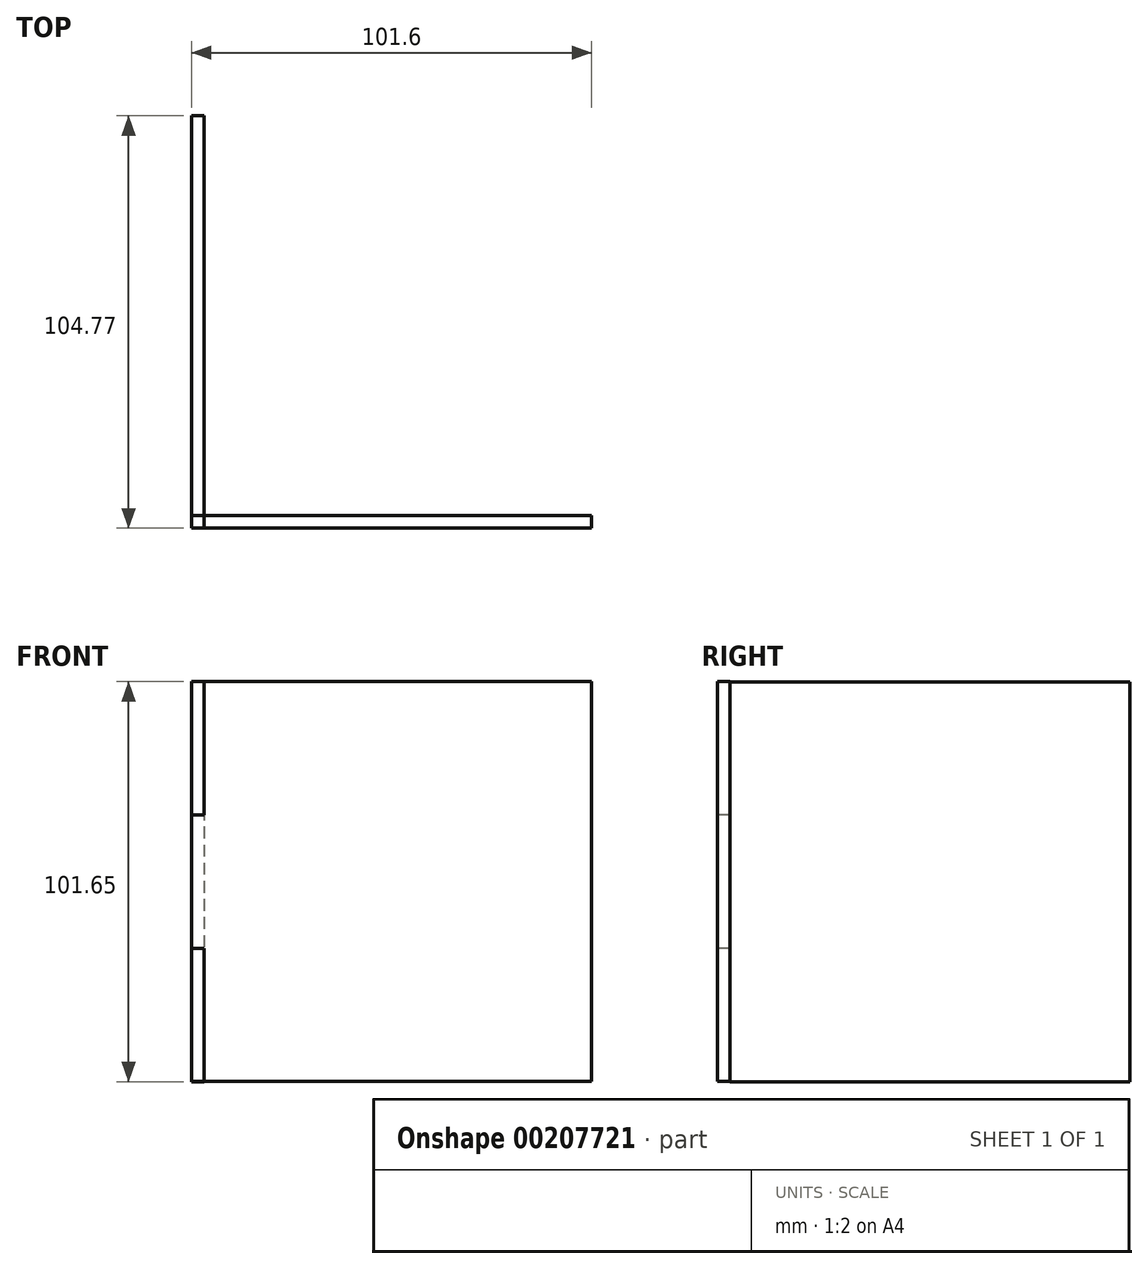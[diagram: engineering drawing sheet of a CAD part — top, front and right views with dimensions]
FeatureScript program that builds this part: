
annotation { "Feature Type Name" : "Feature", "Feature Type Description" : "" }
export const myFeature = defineFeature(function(context is Context, id is Id, definition is map)
    precondition{}
    {
        {
            var Q0;
            Q0=qCreatedBy(makeId("Front.planeOp"),FACE);
            var sketch = newSketch(context, id + "F0", { "sketchPlane" : qUnion([Q0])});
            skLineSegment(sketch, "E0.bottom", {"start": v(0, 50.8) * mm, "end": v(101.6, 50.8) * mm});
            skLineSegment(sketch, "E0.top", {"start": v(0, -50.8) * mm, "end": v(101.6, -50.8) * mm});
            skLineSegment(sketch, "E0.left", {"start": v(0, 50.8) * mm, "end": v(0, -50.8) * mm});
            skLineSegment(sketch, "E0.right", {"start": v(101.6, 50.8) * mm, "end": v(101.6, -50.8) * mm});
            skLineSegment(sketch, "E1.bottom", {"start": v(0, 50.8) * mm, "end": v(0, 50.8) * mm});
            skLineSegment(sketch, "E1.top", {"start": v(0, 0) * mm, "end": v(0, 0) * mm});
            skLineSegment(sketch, "E1.left", {"start": v(0, 50.8) * mm, "end": v(0, 0) * mm});
            skLineSegment(sketch, "E1.right", {"start": v(0, 50.8) * mm, "end": v(0, 0) * mm});
            skSolve(sketch);
        }
        {
            var Q0;
            Q0=makeQuery(id+"F0.imprint","IMPRINT",FACE,{"disambiguationData":[TD([[makeQuery(id+"F0.imprint","IMPRINT",EDGE,{"derivedFrom":sQuery(id+"F0.wireOp",EDGE,"E0.bottom")}),-1.0]])]});
            extrude(context, id + "F1", {"entities" : qUnion([Q0]), "depth" : 3.17 * mm});
        }
        {
            var Q0;
            Q0=qCreatedBy(makeId("Right.planeOp"),FACE);
            var sketch = newSketch(context, id + "F2", { "sketchPlane" : qUnion([Q0])});
            skLineSegment(sketch, "E2.bottom", {"start": v(0, 50.75) * mm, "end": v(101.6, 50.75) * mm});
            skLineSegment(sketch, "E2.top", {"start": v(0, -50.85) * mm, "end": v(101.6, -50.85) * mm});
            skLineSegment(sketch, "E2.left", {"start": v(0, 50.75) * mm, "end": v(0, -50.85) * mm});
            skLineSegment(sketch, "E2.right", {"start": v(101.6, 50.75) * mm, "end": v(101.6, -50.85) * mm});
            skSolve(sketch);
        }
        {
            var Q0;
            Q0=makeQuery(id+"F2.imprint","IMPRINT",FACE,{"disambiguationData":[TD([[makeQuery(id+"F2.imprint","IMPRINT",EDGE,{"derivedFrom":sQuery(id+"F2.wireOp",EDGE,"E2.bottom")}),-1.0]])]});
            extrude(context, id + "F3", {"entities" : qUnion([Q0]), "depth" : 3.17 * mm});
        }
        {
            var Q0;
            Q0=makeQuery(id+"F1.opExtrude","SWEPT_FACE",FACE,{"disambiguationData":[OSD([sQuery(id+"F0.wireOp",EDGE,"E0.left"),sQuery(id+"F0.wireOp",EDGE,"E1.right")])]});
            var sketch = newSketch(context, id + "F4", { "sketchPlane" : qUnion([Q0])});
            skLineSegment(sketch, "E3.bottom", {"start": v(0, -50.8) * mm, "end": v(3.18, -50.8) * mm});
            skLineSegment(sketch, "E3.top", {"start": v(0, -16.93) * mm, "end": v(3.18, -16.93) * mm});
            skLineSegment(sketch, "E3.left", {"start": v(0, -50.8) * mm, "end": v(0, -16.93) * mm});
            skLineSegment(sketch, "E3.right", {"start": v(3.18, -50.8) * mm, "end": v(3.18, -16.93) * mm});
            skLineSegment(sketch, "E4.top", {"start": v(0, 16.93) * mm, "end": v(3.18, 16.93) * mm});
            skLineSegment(sketch, "E4.left", {"start": v(0, -16.93) * mm, "end": v(0, 16.93) * mm});
            skLineSegment(sketch, "E4.right", {"start": v(3.18, -16.93) * mm, "end": v(3.18, 16.93) * mm});
            skLineSegment(sketch, "E5.top", {"start": v(0, 50.8) * mm, "end": v(3.18, 50.8) * mm});
            skLineSegment(sketch, "E5.left", {"start": v(0, 16.93) * mm, "end": v(0, 50.8) * mm});
            skLineSegment(sketch, "E5.right", {"start": v(3.18, 16.93) * mm, "end": v(3.18, 50.8) * mm});
            skSolve(sketch);
        }
        {
            var Q0;
            Q0=makeQuery(id+"F4.imprint","IMPRINT",FACE,{"disambiguationData":[TD([[makeQuery(id+"F4.imprint","IMPRINT",EDGE,{"derivedFrom":sQuery(id+"F4.wireOp",EDGE,"E3.bottom")}),-1.0]])]});
            var Q1;
            Q1=makeQuery(id+"F4.imprint","IMPRINT",FACE,{"disambiguationData":[TD([[makeQuery(id+"F4.imprint","IMPRINT",EDGE,{"derivedFrom":sQuery(id+"F4.wireOp",EDGE,"E4.top")}),1.0]])]});
            extrude(context, id + "F5", {"entities" : qUnion([Q0, Q1]), "oppositeDirection" : true, "depth" : 3.17 * mm});
        }
        {
            var Q0;
            Q0=makeQuery(id+"F5.opExtrude","SWEPT_BODY",BODY,{"disambiguationData":[OSD([sQuery(id+"F4.wireOp",EDGE,"E4.top"),sQuery(id+"F4.wireOp",EDGE,"E5.top"),sQuery(id+"F4.wireOp",EDGE,"E5.left"),sQuery(id+"F4.wireOp",EDGE,"E5.right")])]});
            var Q1;
            Q1=makeQuery(id+"F5.opExtrude","SWEPT_BODY",BODY,{"disambiguationData":[OSD([sQuery(id+"F4.wireOp",EDGE,"E3.bottom"),sQuery(id+"F4.wireOp",EDGE,"E3.left"),sQuery(id+"F4.wireOp",EDGE,"E3.right"),sQuery(id+"F4.wireOp",EDGE,"E3.top")])]});
            var Q2;
            Q2=makeQuery(id+"F1.opExtrude","SWEPT_BODY",BODY,{"disambiguationData":[OSD([sQuery(id+"F0.wireOp",EDGE,"E0.bottom"),sQuery(id+"F0.wireOp",EDGE,"E0.top"),sQuery(id+"F0.wireOp",EDGE,"E0.left"),sQuery(id+"F0.wireOp",EDGE,"E0.right"),sQuery(id+"F0.wireOp",EDGE,"E1.right")])]});
            booleanBodies(context, id + "F6", {"operationType" : BooleanOperationType.SUBTRACTION, "tools" : qUnion([Q0, Q1]), "targets" : qUnion([Q2]), "keepTools" : true});
        }
    });
